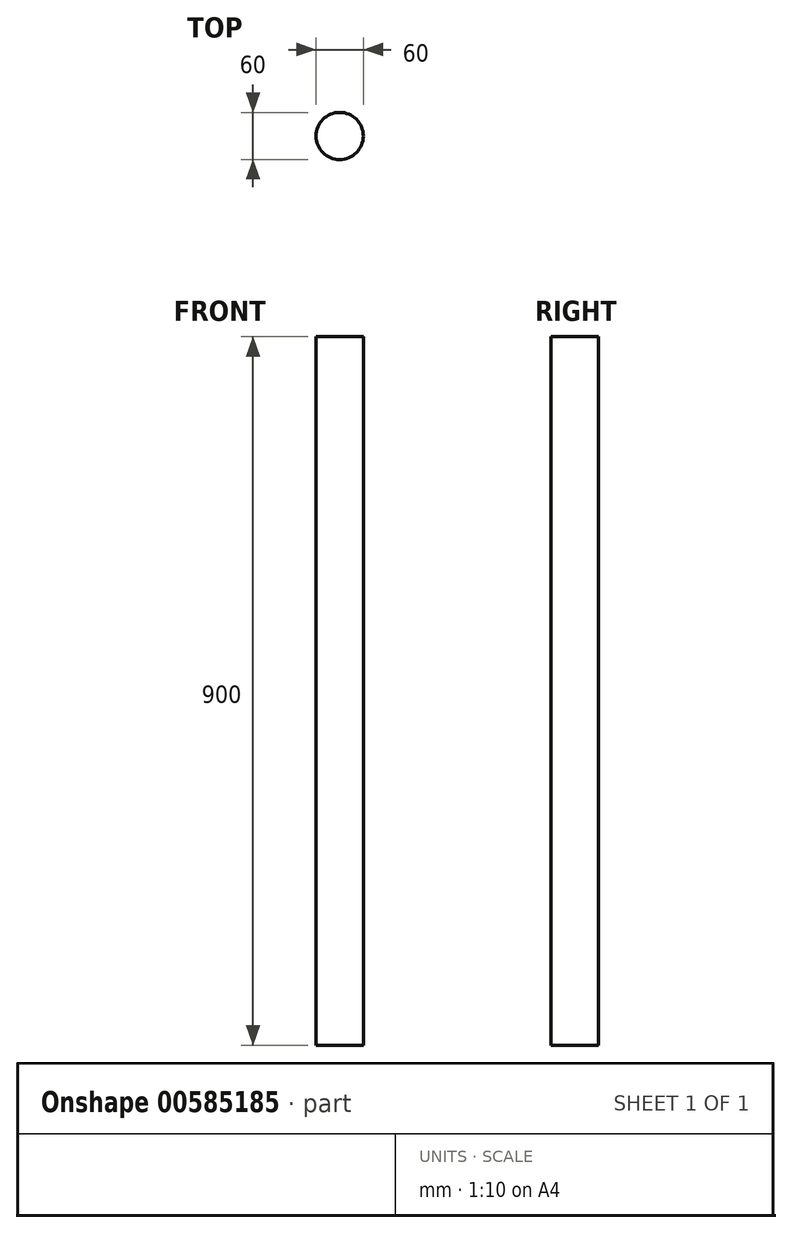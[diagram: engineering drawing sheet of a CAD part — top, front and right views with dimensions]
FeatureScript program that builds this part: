
annotation { "Feature Type Name" : "Feature", "Feature Type Description" : "" }
export const myFeature = defineFeature(function(context is Context, id is Id, definition is map)
    precondition{}
    {
        {
            var Q0;
            Q0=qCreatedBy(makeId("Top.planeOp"),FACE);
            var sketch = newSketch(context, id + "F0", { "sketchPlane" : qUnion([Q0])});
            skCircle(sketch, "E0", {"center": v(0, 0) * mm, "radius": 30 * mm});
            skSolve(sketch);
        }
        {
            var Q0;
            Q0 = qSketchRegion(id + "F0", true);
            extrude(context, id + "F1", {"entities" : qUnion([Q0]), "depth" : 900 * mm, "offsetDistance" : 25 * mm});
        }
    });
